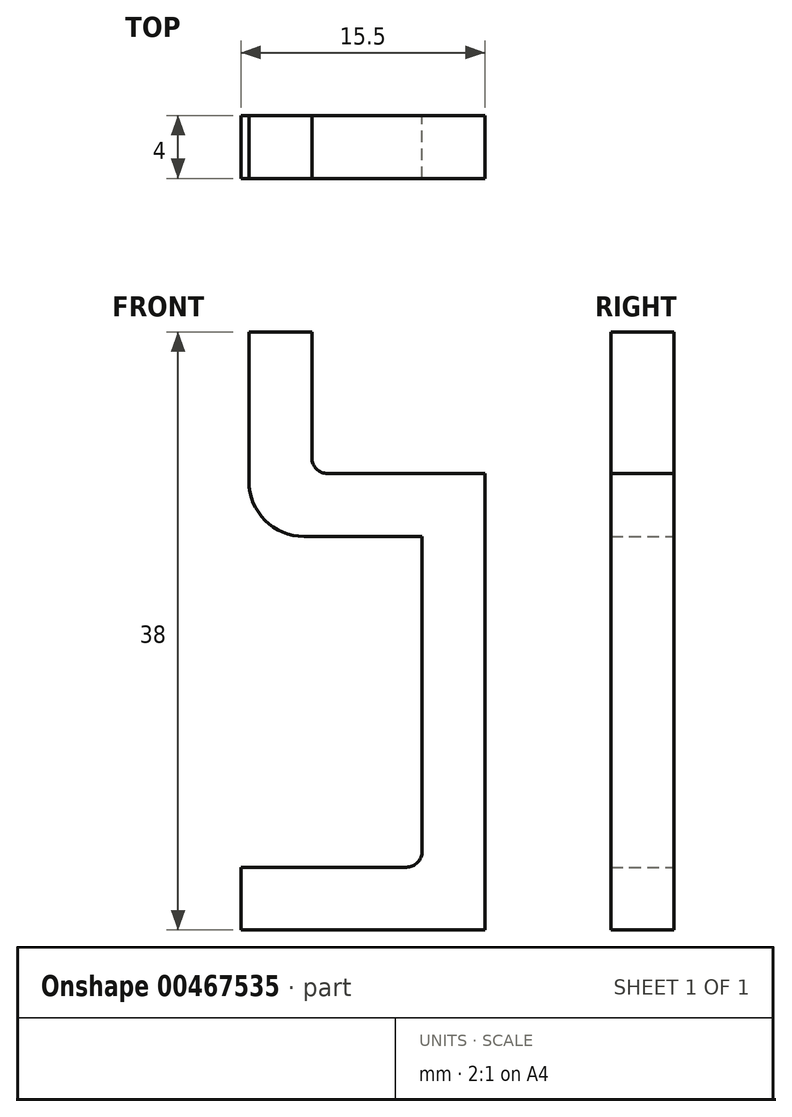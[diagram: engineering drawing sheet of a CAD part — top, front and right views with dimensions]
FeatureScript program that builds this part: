
annotation { "Feature Type Name" : "Feature", "Feature Type Description" : "" }
export const myFeature = defineFeature(function(context is Context, id is Id, definition is map)
    precondition{}
    {
        {
            var Q0;
            Q0=qCreatedBy(makeId("Front.planeOp"),FACE);
            var sketch = newSketch(context, id + "F0", { "sketchPlane" : qUnion([Q0])});
            skLineSegment(sketch, "E0", {"start": v(0, 0) * mm, "end": v(-13.5, 0) * mm});
            skLineSegment(sketch, "E1", {"start": v(0, 0) * mm, "end": v(0, 25) * mm});
            skLineSegment(sketch, "E2", {"start": v(0, 25) * mm, "end": v(-11, 25) * mm});
            skLineSegment(sketch, "E3", {"start": v(-11, 25) * mm, "end": v(-11, 36) * mm});
            skSolve(sketch);
        }
        {
            var Q0;
            Q0=sQuery(id+"F0.wireOp",EDGE,"E0");
            var Q1;
            Q1=sQuery(id+"F0.wireOp",VERTEX,"E0.end");
            cPlane(context, id + "F1", {"entities" : qUnion([Q0, Q1]), "cplaneType" : CPlaneType.LINE_POINT, "offset" : 25 * mm, "width" : 150 * mm, "height" : 150 * mm});
        }
        {
            var Q0;
            Q0=qCreatedBy(id+"F1.planeOp",FACE);
            var sketch = newSketch(context, id + "F2", { "sketchPlane" : qUnion([Q0])});
            skLineSegment(sketch, "E4.bottom", {"start": v(2, 2) * mm, "end": v(-2, 2) * mm});
            skLineSegment(sketch, "E4.top", {"start": v(2, -2) * mm, "end": v(-2, -2) * mm});
            skLineSegment(sketch, "E4.left", {"start": v(2, 2) * mm, "end": v(2, -2) * mm});
            skLineSegment(sketch, "E4.right", {"start": v(-2, 2) * mm, "end": v(-2, -2) * mm});
            skPoint(sketch, "E4.middle", {"position": v(0, 0) * mm});
            skSolve(sketch);
        }
        {
            var Q0;
            Q0=makeQuery(id+"F2.imprint","IMPRINT",FACE,{"disambiguationData":[TD([[makeQuery(id+"F2.imprint","IMPRINT",EDGE,{"derivedFrom":sQuery(id+"F2.wireOp",EDGE,"E4.bottom")}),1.0]])]});
            var Q1;
            Q1=sQuery(id+"F0.wireOp",EDGE,"E0");
            var Q2;
            Q2=sQuery(id+"F0.wireOp",EDGE,"E1");
            var Q3;
            Q3=sQuery(id+"F0.wireOp",EDGE,"E2");
            var Q4;
            Q4=sQuery(id+"F0.wireOp",EDGE,"E3");
            sweep(context, id + "F3", {"profiles" : qUnion([Q0]), "path" : qUnion([Q1, Q2, Q3, Q4])});
        }
        {
            var Q0;
            Q0=makeQuery(id+"F3.opSweep","MID_CAP_EDGE",EDGE,{"disambiguationData":[OSD([sQuery(id+"F0.wireOp",VERTEX,"E3.start"),sQuery(id+"F2.wireOp",EDGE,"E4.bottom")])],"capPos":3.0});
            fillet(context, id + "F4", {"entities" : qUnion([Q0]), "radius" : 3.5 * mm, "tangentPropagation" : true, "allowEdgeOverflow" : false});
        }
        {
            var Q0;
            Q0=makeQuery(id+"F3.opSweep","MID_CAP_EDGE",EDGE,{"disambiguationData":[OSD([sQuery(id+"F0.wireOp",VERTEX,"E3.start"),sQuery(id+"F2.wireOp",EDGE,"E4.top")])],"capPos":3.0});
            var Q1;
            Q1=makeQuery(id+"F3.opSweep","MID_CAP_EDGE",EDGE,{"disambiguationData":[OSD([sQuery(id+"F0.wireOp",VERTEX,"E1.start"),sQuery(id+"F2.wireOp",EDGE,"E4.bottom")])],"capPos":1.0});
            fillet(context, id + "F5", {"entities" : qUnion([Q0, Q1]), "radius" : 1 * mm, "tangentPropagation" : true, "allowEdgeOverflow" : false});
        }
    });
